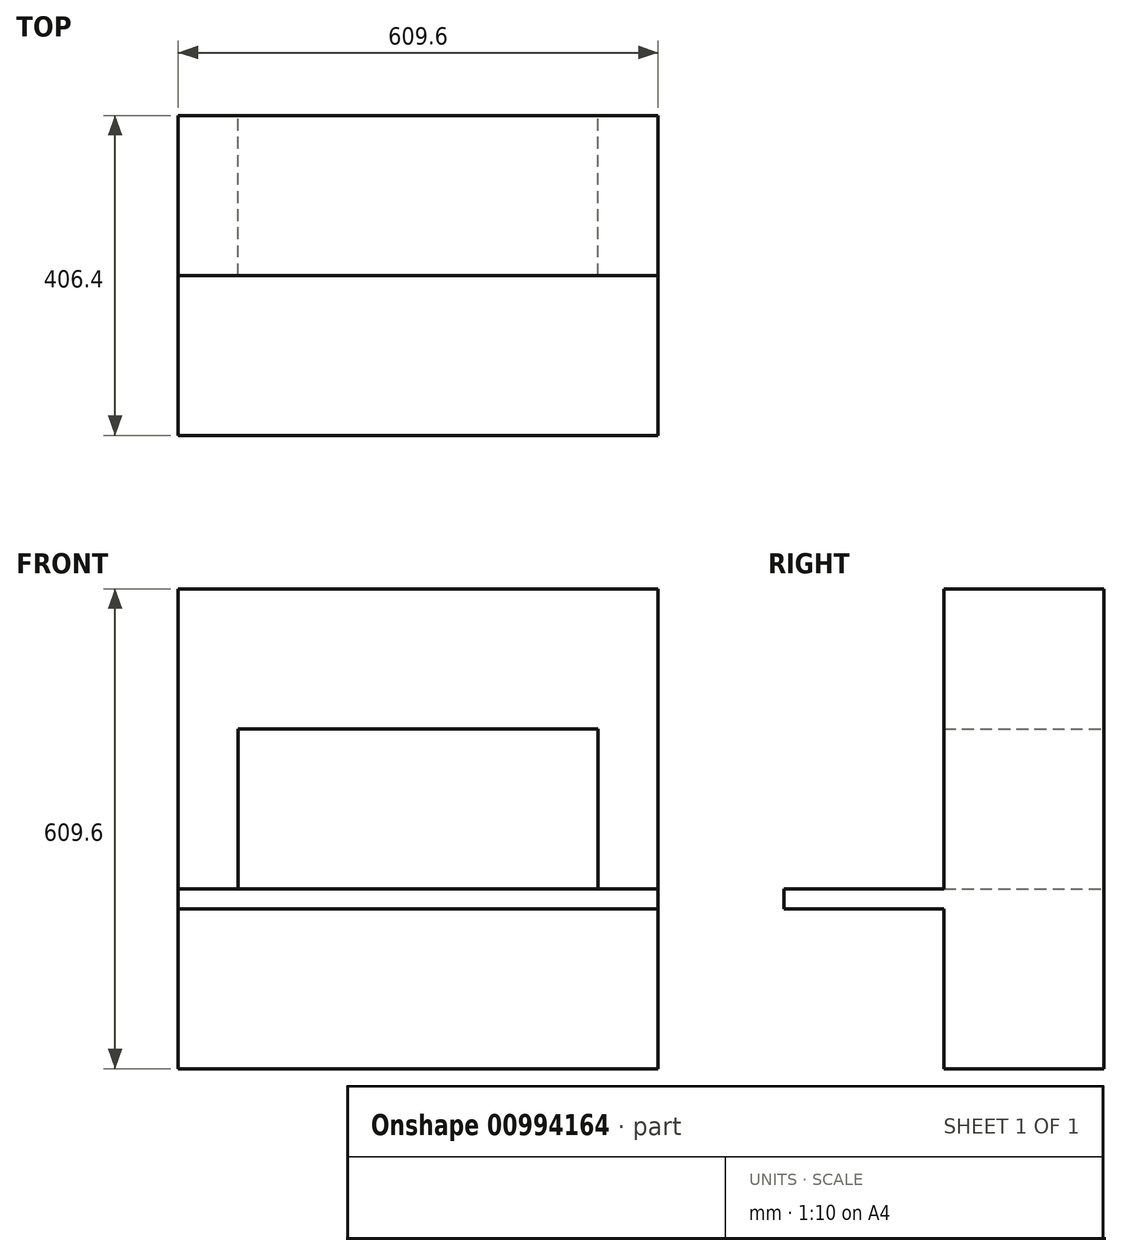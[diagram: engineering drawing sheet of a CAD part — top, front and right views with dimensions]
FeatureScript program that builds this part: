
annotation { "Feature Type Name" : "Feature", "Feature Type Description" : "" }
export const myFeature = defineFeature(function(context is Context, id is Id, definition is map)
    precondition{}
    {
        {
            var Q0;
            Q0=qCreatedBy(makeId("Front.planeOp"),FACE);
            var sketch = newSketch(context, id + "F0", { "sketchPlane" : qUnion([Q0])});
            skLineSegment(sketch, "E0.bottom", {"start": v(0, 488.92) * mm, "end": v(457.2, 488.92) * mm});
            skLineSegment(sketch, "E0.top", {"start": v(0, 285.72) * mm, "end": v(457.2, 285.72) * mm});
            skLineSegment(sketch, "E0.left", {"start": v(0, 488.92) * mm, "end": v(0, 285.72) * mm});
            skLineSegment(sketch, "E0.right", {"start": v(457.2, 488.92) * mm, "end": v(457.2, 285.72) * mm});
            skLineSegment(sketch, "E1.bottom", {"start": v(533.4, 57.12) * mm, "end": v(-76.2, 57.12) * mm});
            skLineSegment(sketch, "E1.top", {"start": v(533.4, 666.72) * mm, "end": v(-76.2, 666.72) * mm});
            skLineSegment(sketch, "E1.left", {"start": v(533.4, 57.12) * mm, "end": v(533.4, 666.72) * mm});
            skLineSegment(sketch, "E1.right", {"start": v(-76.2, 57.12) * mm, "end": v(-76.2, 666.72) * mm});
            skSolve(sketch);
        }
        {
            var Q0;
            Q0 = qSketchRegion(id + "F0", true);
            extrude(context, id + "F1", {"entities" : qUnion([Q0]), "depth" : 203.2 * mm, "offsetDistance" : 25.4 * mm});
        }
        {
            var Q0;
            Q0=makeQuery(id+"F1.opExtrude","CAP_FACE",FACE,{"disambiguationData":[OSD([sQuery(id+"F0.wireOp",EDGE,"E0.bottom"),sQuery(id+"F0.wireOp",EDGE,"E0.top"),sQuery(id+"F0.wireOp",EDGE,"E0.left"),sQuery(id+"F0.wireOp",EDGE,"E0.right"),sQuery(id+"F0.wireOp",EDGE,"E1.bottom"),sQuery(id+"F0.wireOp",EDGE,"E1.top"),sQuery(id+"F0.wireOp",EDGE,"E1.left"),sQuery(id+"F0.wireOp",EDGE,"E1.right")])],"isStart":false});
            var sketch = newSketch(context, id + "F2", { "sketchPlane" : qUnion([Q0])});
            skLineSegment(sketch, "E2.bottom", {"start": v(-76.2, 285.72) * mm, "end": v(533.4, 285.72) * mm});
            skLineSegment(sketch, "E2.top", {"start": v(-76.2, 260.32) * mm, "end": v(533.4, 260.32) * mm});
            skLineSegment(sketch, "E2.left", {"start": v(-76.2, 285.72) * mm, "end": v(-76.2, 260.32) * mm});
            skLineSegment(sketch, "E2.right", {"start": v(533.4, 285.72) * mm, "end": v(533.4, 260.32) * mm});
            skSolve(sketch);
        }
        {
            var Q0;
            Q0 = qSketchRegion(id + "F2", true);
            extrude(context, id + "F3", {"entities" : qUnion([Q0]), "operationType" : NewBodyOperationType.ADD, "depth" : 203.2 * mm, "offsetDistance" : 25.4 * mm});
        }
    });
